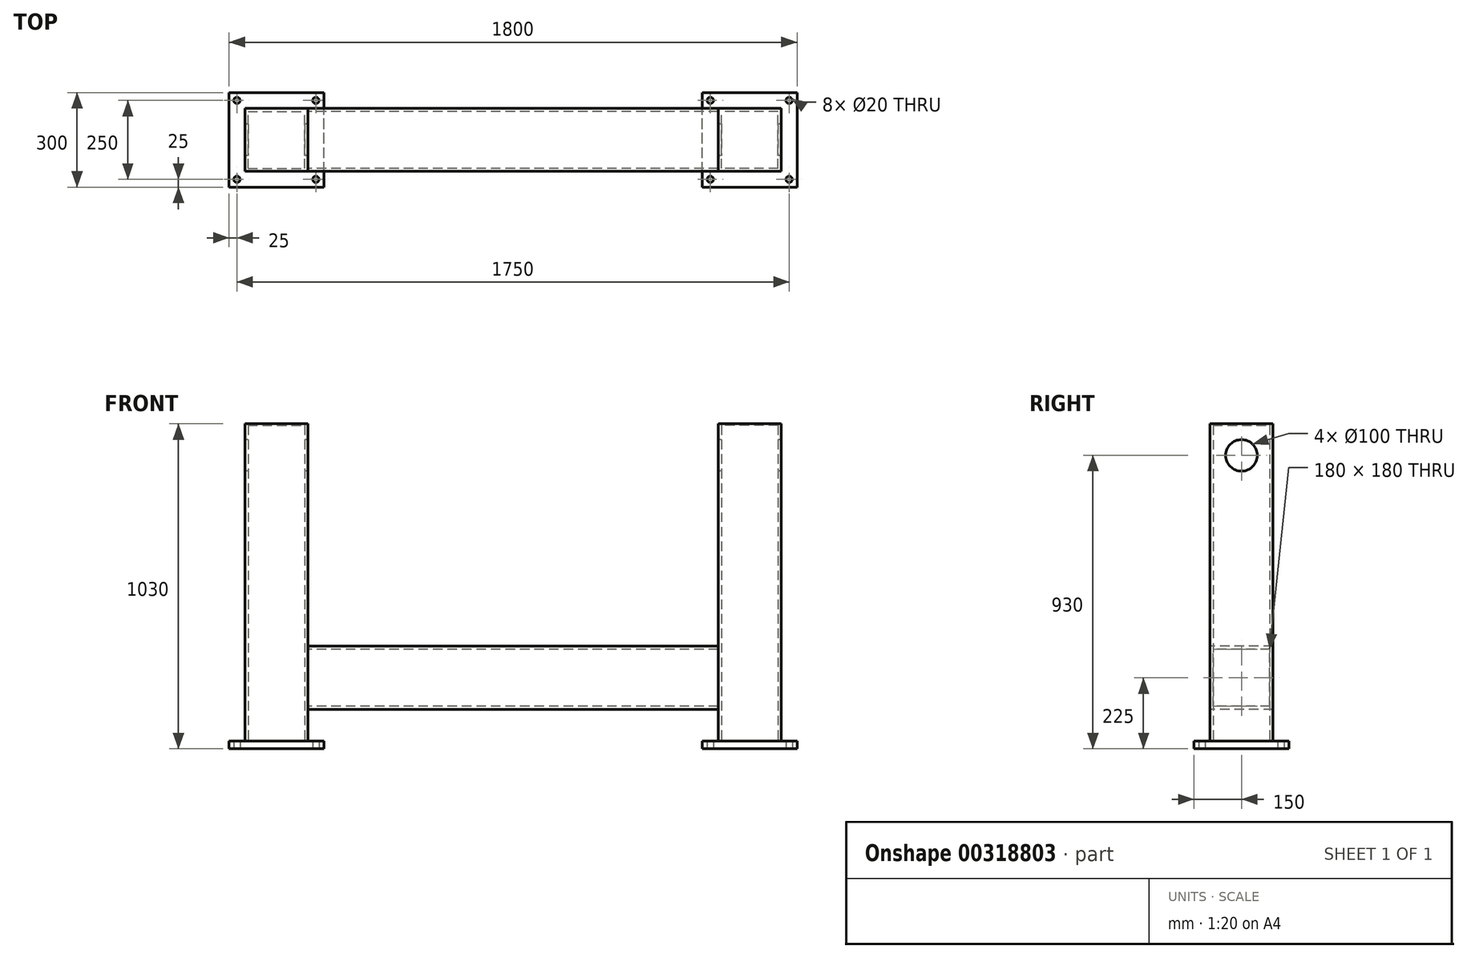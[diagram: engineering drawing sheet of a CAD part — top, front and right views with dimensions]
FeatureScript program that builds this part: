
annotation { "Feature Type Name" : "Feature", "Feature Type Description" : "" }
export const myFeature = defineFeature(function(context is Context, id is Id, definition is map)
    precondition{}
    {
        {
            var Q0;
            Q0=qCreatedBy(makeId("Top.planeOp"),FACE);
            var sketch = newSketch(context, id + "F0", { "sketchPlane" : qUnion([Q0])});
            skLineSegment(sketch, "E0.bottom", {"start": v(-900, -150) * mm, "end": v(-600, -150) * mm});
            skLineSegment(sketch, "E0.top", {"start": v(-900, 150) * mm, "end": v(-600, 150) * mm});
            skLineSegment(sketch, "E0.left", {"start": v(-900, -150) * mm, "end": v(-900, 150) * mm});
            skLineSegment(sketch, "E0.right", {"start": v(-600, -150) * mm, "end": v(-600, 150) * mm});
            skPoint(sketch, "E0.middle", {"position": v(-750, 0) * mm});
            skLineSegment(sketch, "E1.bottom", {"start": v(-875, 125) * mm, "end": v(-625, 125) * mm, "construction": true});
            skLineSegment(sketch, "E1.top", {"start": v(-875, -125) * mm, "end": v(-625, -125) * mm, "construction": true});
            skLineSegment(sketch, "E1.left", {"start": v(-875, 125) * mm, "end": v(-875, -125) * mm, "construction": true});
            skLineSegment(sketch, "E1.right", {"start": v(-625, 125) * mm, "end": v(-625, -125) * mm, "construction": true});
            skCircle(sketch, "E2", {"center": v(-625, 125) * mm, "radius": 10 * mm});
            skCircle(sketch, "E3", {"center": v(-875, 125) * mm, "radius": 10 * mm});
            skCircle(sketch, "E4", {"center": v(-875, -125) * mm, "radius": 10 * mm});
            skCircle(sketch, "E5", {"center": v(-625, -125) * mm, "radius": 10 * mm});
            skCircle(sketch, "E6.MirrorC", {"center": v(625, -125) * mm, "radius": 10 * mm});
            skCircle(sketch, "E7.MirrorC", {"center": v(875, -125) * mm, "radius": 10 * mm});
            skCircle(sketch, "E8.MirrorC", {"center": v(875, 125) * mm, "radius": 10 * mm});
            skCircle(sketch, "E9.MirrorC", {"center": v(625, 125) * mm, "radius": 10 * mm});
            skLineSegment(sketch, "E10.MirrorCS", {"start": v(900, -150) * mm, "end": v(600, -150) * mm});
            skPoint(sketch, "E11.MirrorP", {"position": v(750, 0) * mm});
            skLineSegment(sketch, "E12.MirrorCS", {"start": v(875, -125) * mm, "end": v(625, -125) * mm, "construction": true});
            skLineSegment(sketch, "E13.MirrorCS", {"start": v(900, 150) * mm, "end": v(600, 150) * mm});
            skLineSegment(sketch, "E14.MirrorCS", {"start": v(900, -150) * mm, "end": v(900, 150) * mm});
            skLineSegment(sketch, "E15.MirrorCS", {"start": v(600, -150) * mm, "end": v(600, 150) * mm});
            skLineSegment(sketch, "E16.MirrorCS", {"start": v(875, 125) * mm, "end": v(625, 125) * mm, "construction": true});
            skLineSegment(sketch, "E17.MirrorCS", {"start": v(875, 125) * mm, "end": v(875, -125) * mm, "construction": true});
            skLineSegment(sketch, "E18.MirrorCS", {"start": v(625, 125) * mm, "end": v(625, -125) * mm, "construction": true});
            skSolve(sketch);
        }
        {
            var Q0;
            Q0=qSketchRegion(id+"F0",true);
            extrude(context, id + "F1", {"entities" : qUnion([Q0]), "depth" : 25 * mm});
        }
        {
            var Q0;
            Q0=makeQuery(id+"F1.opExtrude","CAP_FACE",FACE,{"disambiguationData":[OSD([sQuery(id+"F0.wireOp",EDGE,"E0.bottom"),sQuery(id+"F0.wireOp",EDGE,"E0.top"),sQuery(id+"F0.wireOp",EDGE,"E0.left"),sQuery(id+"F0.wireOp",EDGE,"E0.right"),sQuery(id+"F0.wireOp",EDGE,"E2"),sQuery(id+"F0.wireOp",EDGE,"E3"),sQuery(id+"F0.wireOp",EDGE,"E4"),sQuery(id+"F0.wireOp",EDGE,"E5")])],"isStart":false});
            var sketch = newSketch(context, id + "F2", { "sketchPlane" : qUnion([Q0])});
            skLineSegment(sketch, "E19.bottom", {"start": v(-850, -100) * mm, "end": v(-650, -100) * mm});
            skLineSegment(sketch, "E19.top", {"start": v(-850, 100) * mm, "end": v(-650, 100) * mm});
            skLineSegment(sketch, "E19.left", {"start": v(-850, -100) * mm, "end": v(-850, 100) * mm});
            skLineSegment(sketch, "E19.right", {"start": v(-650, -100) * mm, "end": v(-650, 100) * mm});
            skPoint(sketch, "E19.middle", {"position": v(-750, 0) * mm});
            skPoint(sketch, "E19.middle.positionSnap0", {"position": v(-750, -150) * mm});
            skPoint(sketch, "E19.centerSnap0", {"position": v(-750, -150) * mm});
            skLineSegment(sketch, "E20.bottom", {"start": v(-840, -90) * mm, "end": v(-660, -90) * mm});
            skLineSegment(sketch, "E20.top", {"start": v(-840, 90) * mm, "end": v(-660, 90) * mm});
            skLineSegment(sketch, "E20.left", {"start": v(-840, -90) * mm, "end": v(-840, 90) * mm});
            skLineSegment(sketch, "E20.right", {"start": v(-660, -90) * mm, "end": v(-660, 90) * mm});
            skPoint(sketch, "E21.MirrorP", {"position": v(750, -150) * mm});
            skPoint(sketch, "E22.MirrorP", {"position": v(750, 0) * mm});
            skLineSegment(sketch, "E23.MirrorCS", {"start": v(850, -100) * mm, "end": v(650, -100) * mm});
            skLineSegment(sketch, "E24.MirrorCS", {"start": v(850, 100) * mm, "end": v(650, 100) * mm});
            skLineSegment(sketch, "E25.MirrorCS", {"start": v(850, -100) * mm, "end": v(850, 100) * mm});
            skLineSegment(sketch, "E26.MirrorCS", {"start": v(650, -100) * mm, "end": v(650, 100) * mm});
            skLineSegment(sketch, "E27.MirrorCS", {"start": v(840, -90) * mm, "end": v(660, -90) * mm});
            skLineSegment(sketch, "E28.MirrorCS", {"start": v(660, -90) * mm, "end": v(660, 90) * mm});
            skLineSegment(sketch, "E29.MirrorCS", {"start": v(840, -90) * mm, "end": v(840, 90) * mm});
            skLineSegment(sketch, "E30.MirrorCS", {"start": v(840, 90) * mm, "end": v(660, 90) * mm});
            skSolve(sketch);
        }
        {
            var Q0;
            Q0=qSketchRegion(id+"F2",true);
            extrude(context, id + "F3", {"entities" : qUnion([Q0]), "depth" : 1000 * mm});
        }
        {
            var Q0;
            Q0=makeQuery(id+"F3.opExtrude","SWEPT_FACE",FACE,{"disambiguationData":[OSD([sQuery(id+"F2.wireOp",EDGE,"E19.right")])]});
            var sketch = newSketch(context, id + "F4", { "sketchPlane" : qUnion([Q0])});
            skLineSegment(sketch, "E31.bottom", {"start": v(-100, 325) * mm, "end": v(100, 325) * mm});
            skLineSegment(sketch, "E31.top", {"start": v(-100, 125) * mm, "end": v(100, 125) * mm});
            skLineSegment(sketch, "E31.left", {"start": v(-100, 325) * mm, "end": v(-100, 125) * mm});
            skLineSegment(sketch, "E31.right", {"start": v(100, 325) * mm, "end": v(100, 125) * mm});
            skLineSegment(sketch, "E32.bottom", {"start": v(-90, 315) * mm, "end": v(90, 315) * mm});
            skLineSegment(sketch, "E32.top", {"start": v(-90, 135) * mm, "end": v(90, 135) * mm});
            skLineSegment(sketch, "E32.left", {"start": v(-90, 315) * mm, "end": v(-90, 135) * mm});
            skLineSegment(sketch, "E32.right", {"start": v(90, 315) * mm, "end": v(90, 135) * mm});
            skSolve(sketch);
        }
        {
            var Q0;
            Q0=qSketchRegion(id+"F4",true);
            var Q1;
            Q1=makeQuery(id+"F4.imprint","IMPRINT",FACE,{"disambiguationData":[TD([[makeQuery(id+"F4.imprint","IMPRINT",EDGE,{"derivedFrom":sQuery(id+"F4.wireOp",EDGE,"E31.bottom")}),-1.0]])]});
            var Q2;
            Q2=makeQuery(id+"F3.opExtrude","SWEPT_BODY",BODY,{"disambiguationData":[OSD([sQuery(id+"F2.wireOp",EDGE,"E23.MirrorCS"),sQuery(id+"F2.wireOp",EDGE,"E24.MirrorCS"),sQuery(id+"F2.wireOp",EDGE,"E25.MirrorCS"),sQuery(id+"F2.wireOp",EDGE,"E26.MirrorCS"),sQuery(id+"F2.wireOp",EDGE,"E27.MirrorCS"),sQuery(id+"F2.wireOp",EDGE,"E28.MirrorCS"),sQuery(id+"F2.wireOp",EDGE,"E29.MirrorCS"),sQuery(id+"F2.wireOp",EDGE,"E30.MirrorCS")])]});
            extrude(context, id + "F5", {"entities" : qUnion([Q0, Q1]), "endBound" : BoundingType.UP_TO_BODY, "endBoundEntityBody" : qUnion([Q2]), "depth" : 25 * mm});
        }
        {
            var Q0;
            Q0=makeQuery(id+"F3.opExtrude","CAP_FACE",FACE,{"disambiguationData":[OSD([sQuery(id+"F2.wireOp",EDGE,"E19.bottom"),sQuery(id+"F2.wireOp",EDGE,"E19.top"),sQuery(id+"F2.wireOp",EDGE,"E19.left"),sQuery(id+"F2.wireOp",EDGE,"E19.right"),sQuery(id+"F2.wireOp",EDGE,"E20.bottom"),sQuery(id+"F2.wireOp",EDGE,"E20.top"),sQuery(id+"F2.wireOp",EDGE,"E20.left"),sQuery(id+"F2.wireOp",EDGE,"E20.right")])],"isStart":false});
            var sketch = newSketch(context, id + "F6", { "sketchPlane" : qUnion([Q0])});
            skLineSegment(sketch, "E33.bottom", {"start": v(-850, 100) * mm, "end": v(-650, 100) * mm});
            skLineSegment(sketch, "E33.top", {"start": v(-850, -100) * mm, "end": v(-650, -100) * mm});
            skLineSegment(sketch, "E33.left", {"start": v(-850, 100) * mm, "end": v(-850, -100) * mm});
            skLineSegment(sketch, "E33.right", {"start": v(-650, 100) * mm, "end": v(-650, -100) * mm});
            skSolve(sketch);
        }
        {
            var Q0;
            Q0=qSketchRegion(id+"F6",true);
            extrude(context, id + "F7", {"entities" : qUnion([Q0]), "operationType" : NewBodyOperationType.ADD, "depth" : 5 * mm});
        }
        {
            var Q0;
            Q0=makeQuery(id+"F3.opExtrude","CAP_FACE",FACE,{"disambiguationData":[OSD([sQuery(id+"F2.wireOp",EDGE,"E23.MirrorCS"),sQuery(id+"F2.wireOp",EDGE,"E24.MirrorCS"),sQuery(id+"F2.wireOp",EDGE,"E25.MirrorCS"),sQuery(id+"F2.wireOp",EDGE,"E26.MirrorCS"),sQuery(id+"F2.wireOp",EDGE,"E27.MirrorCS"),sQuery(id+"F2.wireOp",EDGE,"E28.MirrorCS"),sQuery(id+"F2.wireOp",EDGE,"E29.MirrorCS"),sQuery(id+"F2.wireOp",EDGE,"E30.MirrorCS")])],"isStart":false});
            var sketch = newSketch(context, id + "F8", { "sketchPlane" : qUnion([Q0])});
            skLineSegment(sketch, "E34.bottom", {"start": v(650, 100) * mm, "end": v(850, 100) * mm});
            skLineSegment(sketch, "E34.top", {"start": v(650, -100) * mm, "end": v(850, -100) * mm});
            skLineSegment(sketch, "E34.left", {"start": v(650, 100) * mm, "end": v(650, -100) * mm});
            skLineSegment(sketch, "E34.right", {"start": v(850, 100) * mm, "end": v(850, -100) * mm});
            skSolve(sketch);
        }
        {
            var Q0;
            Q0=qSketchRegion(id+"F8",true);
            extrude(context, id + "F9", {"entities" : qUnion([Q0]), "operationType" : NewBodyOperationType.ADD, "depth" : 5 * mm});
        }
        {
            var Q0;
            Q0=makeQuery(id+"F7.boolean.opBoolean","MERGE",FACE,{"derivedFrom":[makeQuery(id+"F3.opExtrude","SWEPT_FACE",FACE,{"disambiguationData":[OSD([sQuery(id+"F2.wireOp",EDGE,"E19.left")])]}),makeQuery(id+"F7.opExtrude","SWEPT_FACE",FACE,{"disambiguationData":[OSD([sQuery(id+"F6.wireOp",EDGE,"E33.left")])]})]});
            var sketch = newSketch(context, id + "F10", { "sketchPlane" : qUnion([Q0])});
            skLineSegment(sketch, "E35", {"start": v(0, 1030) * mm, "end": v(0, 930) * mm, "construction": true});
            skCircle(sketch, "E36", {"center": v(0, 930) * mm, "radius": 50 * mm});
            skSolve(sketch);
        }
        {
            var Q0;
            Q0=qSketchRegion(id+"F10",true);
            extrude(context, id + "F11", {"entities" : qUnion([Q0]), "operationType" : NewBodyOperationType.REMOVE, "endBound" : BoundingType.THROUGH_ALL, "oppositeDirection" : true, "depth" : 25 * mm});
        }
    });
